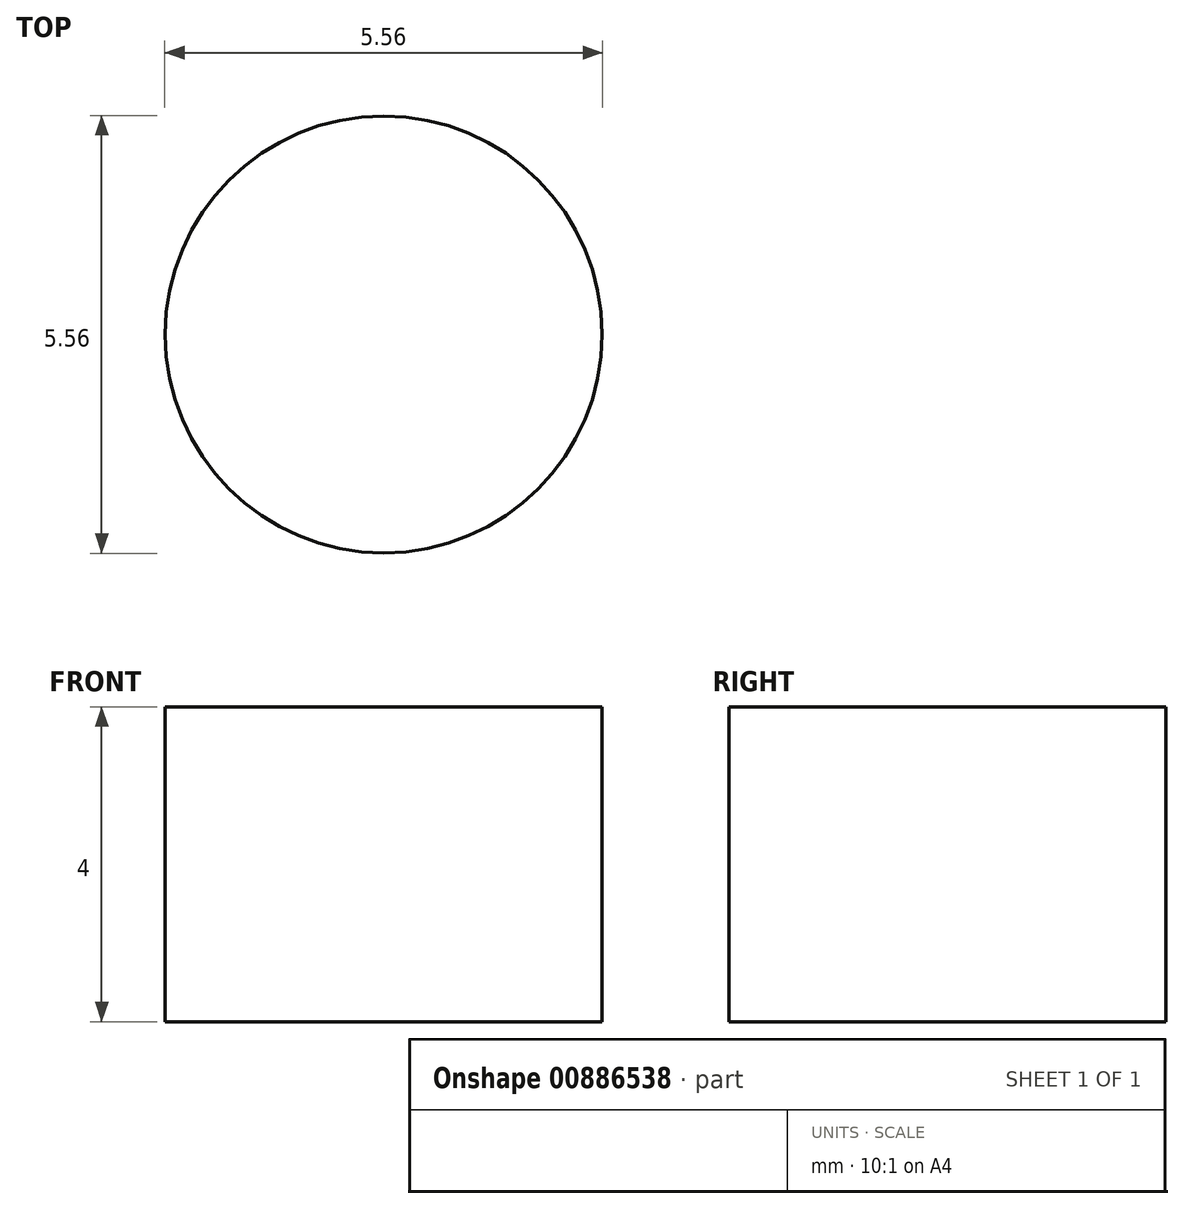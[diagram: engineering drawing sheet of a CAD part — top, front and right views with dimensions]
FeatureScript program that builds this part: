
annotation { "Feature Type Name" : "Feature", "Feature Type Description" : "" }
export const myFeature = defineFeature(function(context is Context, id is Id, definition is map)
    precondition{}
    {
        {
            var Q0;
            Q0=qCreatedBy(makeId("Top.planeOp"),FACE);
            var sketch = newSketch(context, id + "F0", { "sketchPlane" : qUnion([Q0])});
            skCircle(sketch, "E0", {"center": v(0, 0) * mm, "radius": 2.77 * mm});
            skSolve(sketch);
        }
        {
            var Q0;
            Q0 = qSketchRegion(id + "F0", true);
            extrude(context, id + "F1", {"entities" : qUnion([Q0]), "depth" : 4 * mm, "offsetDistance" : 25 * mm});
        }
    });
